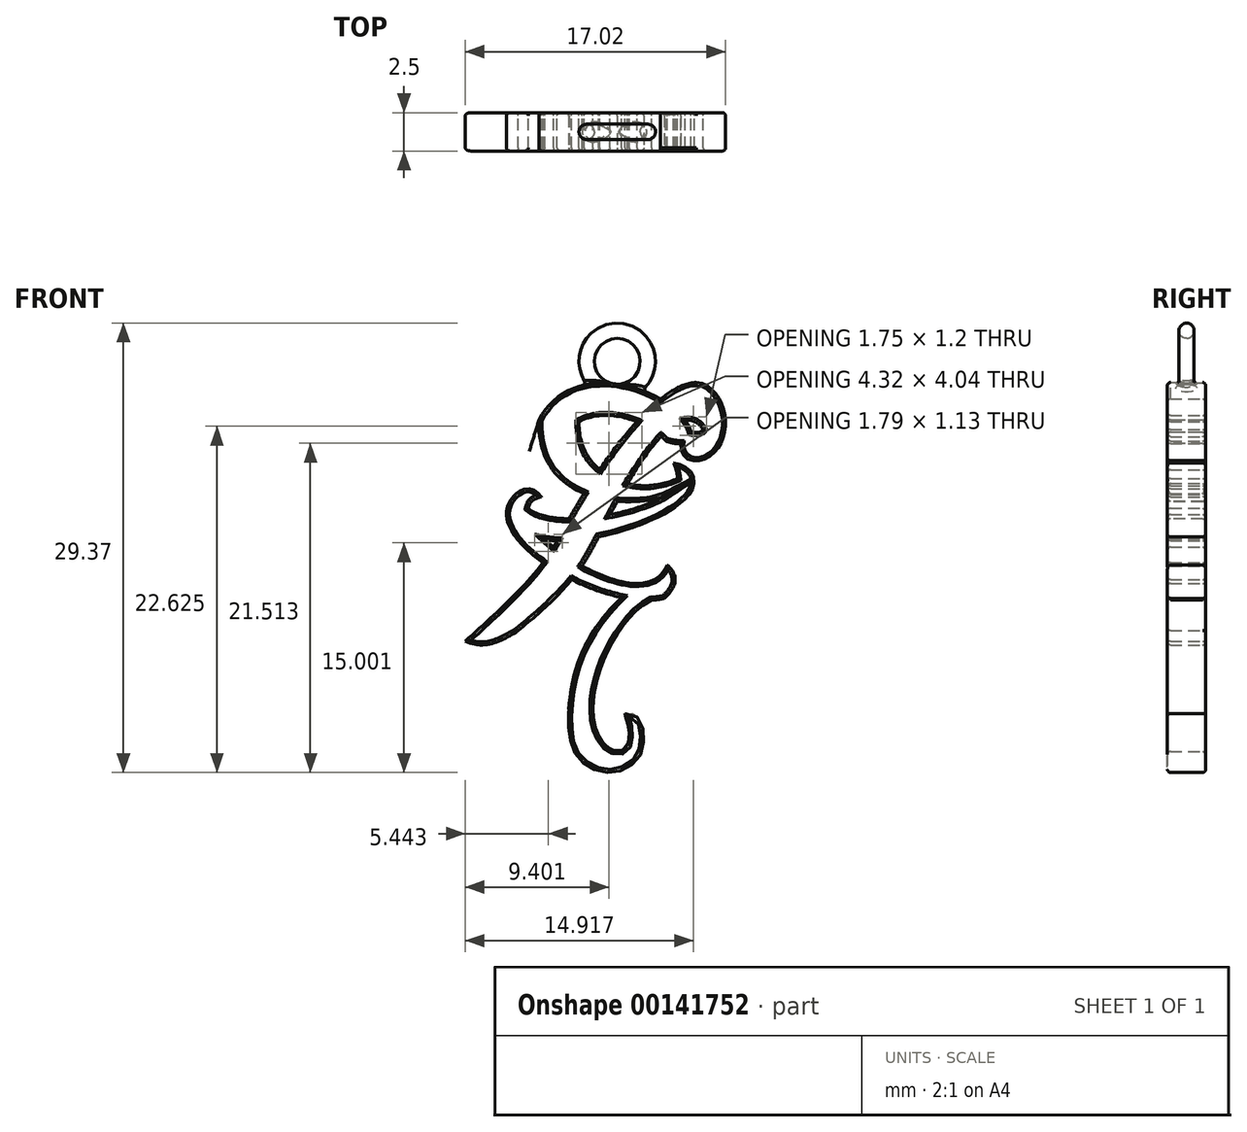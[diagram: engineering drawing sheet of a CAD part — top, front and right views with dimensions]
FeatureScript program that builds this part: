
annotation { "Feature Type Name" : "Feature", "Feature Type Description" : "" }
export const myFeature = defineFeature(function(context is Context, id is Id, definition is map)
    precondition{}
    {
        {
            var Q0;
            Q0=qCreatedBy(makeId("Front.planeOp"),FACE);
            var sketch = newSketch(context, id + "F0", { "sketchPlane" : qUnion([Q0])});
            skLineSegment(sketch, "E0.bottom", {"start": v(0, 0) * mm, "end": v(12.5, 0) * mm, "construction": true});
            skLineSegment(sketch, "E0.top", {"start": v(0, 25.5) * mm, "end": v(12.5, 25.5) * mm, "construction": true});
            skLineSegment(sketch, "E0.left", {"start": v(0, 0) * mm, "end": v(0, 25.5) * mm, "construction": true});
            skLineSegment(sketch, "E0.right", {"start": v(12.5, 0) * mm, "end": v(12.5, 25.5) * mm, "construction": true});
            skFitSpline(sketch, "E1", {"points": [v(0.5, 3.96) * mm, v(1.7, 1.95) * mm, v(0.92, 0.6) * mm, v(-0.5, 0.13) * mm, v(-2.58, 1.12) * mm, v(-3.17, 4.25) * mm, v(-2.44, 7.64) * mm, v(-1.46, 9.5) * mm, v(0.27, 11.56) * mm], "startDerivative": vector(27.69, 3.67) * mm, "endDerivative": vector(26.54, 27.1) * mm});
            skFitSpline(sketch, "E2", {"points": [v(-4.96, 18.14) * mm, v(-7.16, 17.54) * mm, v(-4.26, 13.45) * mm, v(3.06, 11.5) * mm], "startDerivative": vector(-9.5, 14) * mm, "endDerivative": vector(13.96, 3.31) * mm});
            skFitSpline(sketch, "E3", {"points": [v(3.06, 11.5) * mm, v(3.27, 13.69) * mm], "startDerivative": vector(2.83, 2.53) * mm, "endDerivative": vector(-2.14, 2) * mm});
            skFitSpline(sketch, "E4", {"points": [v(3.27, 13.69) * mm, v(-5.28, 15.92) * mm, v(-5.69, 17.73) * mm, v(-4.96, 18.14) * mm], "startDerivative": vector(-6.62, -15.9) * mm, "endDerivative": vector(7.8, 2.4) * mm});
            skFitSpline(sketch, "E5", {"points": [v(0.5, 3.96) * mm, v(0.46, 1.6) * mm, v(-0.56, 1.7) * mm, v(-1.47, 3.16) * mm, v(-1.45, 5.64) * mm, v(-0.38, 8.55) * mm, v(1.1, 10.57) * mm, v(2.25, 11.38) * mm], "startDerivative": vector(8.39, -21.65) * mm, "endDerivative": vector(12.87, 6.76) * mm});
            skFitSpline(sketch, "E6", {"points": [v(-5.82, 17.38) * mm, v(3.56, 18.52) * mm, v(3.9, 19.64) * mm, v(3.69, 20.36) * mm], "startDerivative": vector(9.43, -7.56) * mm, "endDerivative": vector(-2.6, 7.84) * mm});
            skFitSpline(sketch, "E7", {"points": [v(-4.74, 15.36) * mm, v(4.78, 18.4) * mm, v(3.69, 20.36) * mm], "startDerivative": vector(11.81, -2.43) * mm, "endDerivative": vector(-11.73, 2.21) * mm});
            skFitSpline(sketch, "E8", {"points": [v(3.25, 18.28) * mm, v(-5.12, 23.17) * mm], "startDerivative": vector(-5.6, -2.83) * mm, "endDerivative": vector(0.72, 17.36) * mm});
            skFitSpline(sketch, "E9", {"points": [v(3.95, 19.34) * mm, v(-2.5, 23.06) * mm], "startDerivative": vector(-9.08, -4.14) * mm, "endDerivative": vector(0.34, 10) * mm});
            skFitSpline(sketch, "E10", {"points": [v(-5.12, 23.17) * mm, v(4.83, 22.38) * mm], "startDerivative": vector(7.14, 13.52) * mm, "endDerivative": vector(2.17, -7.79) * mm});
            skFitSpline(sketch, "E11", {"points": [v(-2.5, 23.06) * mm, v(3.17, 21.8) * mm], "startDerivative": vector(5.66, 2.86) * mm, "endDerivative": vector(3.86, -4.07) * mm});
            skFitSpline(sketch, "E12", {"points": [v(3.17, 21.8) * mm, v(4.15, 21.6) * mm], "startDerivative": vector(0.91, -0.36) * mm, "endDerivative": vector(1.08, 0) * mm});
            skFitSpline(sketch, "E13", {"points": [v(4.83, 22.38) * mm, v(5.62, 22.54) * mm], "startDerivative": vector(0.9, -0.04) * mm, "endDerivative": vector(0.4, 0.77) * mm});
            skFitSpline(sketch, "E14", {"points": [v(4.15, 21.6) * mm, v(5.91, 20.7) * mm, v(7.03, 23.56) * mm, v(5.18, 25.62) * mm], "startDerivative": vector(-0.4, -12.26) * mm, "endDerivative": vector(-7.72, 0.04) * mm});
            skFitSpline(sketch, "E15", {"points": [v(5.62, 22.54) * mm, v(-0.36, 17.18) * mm, v(-6.48, 9.4) * mm], "startDerivative": vector(-9.74, 14.63) * mm, "endDerivative": vector(-24.26, -19.86) * mm});
            skFitSpline(sketch, "E16", {"points": [v(5.18, 25.62) * mm, v(-2.88, 17.18) * mm, v(-9.94, 8.7) * mm], "startDerivative": vector(-15.54, -0.02) * mm, "endDerivative": vector(-34.83, -31.36) * mm});
            skFitSpline(sketch, "E17", {"points": [v(-9.94, 8.7) * mm, v(-6.48, 9.4) * mm], "startDerivative": vector(2.4, -0.95) * mm, "endDerivative": vector(5.47, 3.65) * mm});
            skCircle(sketch, "E18", {"center": v(3.32, 3.06) * mm, "radius": 0.4 * mm, "construction": true});
            skSolve(sketch);
        }
        {
            var Q0;
            {var subQ0=sQuery(id+"F0.wireOp",EDGE,"E3");Q0=makeQuery(id+"F0.imprint","IMPRINT",FACE,{"disambiguationData":[TD([[makeQuery(id+"F0.imprint","IMPRINT",EDGE,{"derivedFrom":subQ0}),1.0]])]});}
            var Q1;
            {var subQ0=sQuery(id+"F0.wireOp",EDGE,"E1");Q1=makeQuery(id+"F0.imprint","IMPRINT",FACE,{"disambiguationData":[TD([[makeQuery(id+"F0.imprint","IMPRINT",EDGE,{"derivedFrom":subQ0}),-1.0]])]});}
            var Q2;
            {var subQ5=sQuery(id+"F0.wireOp",EDGE,"E17");Q2=makeQuery(id+"F0.imprint","IMPRINT",FACE,{"disambiguationData":[TD([[makeQuery(id+"F0.imprint","IMPRINT",EDGE,{"derivedFrom":subQ5}),1.0]])]});}
            var Q3;
            {var subQ0=sQuery(id+"F0.wireOp",EDGE,"E16");var subQ1=sQuery(id+"F0.wireOp",EDGE,"E2");var subQ2=makeQuery(id+"F0.imprint","INTERSECT",VERTEX,{"derivedFrom":[subQ1,subQ0]});Q3=makeQuery(id+"F0.imprint","IMPRINT",FACE,{"disambiguationData":[TD([[makeQuery(id+"F0.imprint","IMPRINT",EDGE,{"disambiguationData":[TD([[subQ2,-1.0]])],"derivedFrom":subQ1}),1.0]])]});}
            var Q4;
            {var subQ0=sQuery(id+"F0.wireOp",EDGE,"E4");var subQ5=sQuery(id+"F0.wireOp",EDGE,"E2");var subQ6=makeQuery(id+"F0.imprint","INTERSECT",VERTEX,{"derivedFrom":[subQ5,subQ0]});Q4=makeQuery(id+"F0.imprint","IMPRINT",FACE,{"disambiguationData":[TD([[makeQuery(id+"F0.imprint","IMPRINT",EDGE,{"disambiguationData":[TD([[subQ6,-1.0]])],"derivedFrom":subQ5}),1.0]])]});}
            var Q5;
            {var subQ0=sQuery(id+"F0.wireOp",EDGE,"E6");var subQ1=sQuery(id+"F0.wireOp",EDGE,"E4");var subQ2=makeQuery(id+"F0.imprint","INTERSECT",VERTEX,{"derivedFrom":[subQ1,subQ0]});Q5=makeQuery(id+"F0.imprint","IMPRINT",FACE,{"disambiguationData":[TD([[makeQuery(id+"F0.imprint","IMPRINT",EDGE,{"disambiguationData":[TD([[subQ2,1.0]])],"derivedFrom":subQ1}),-1.0]])]});}
            var Q6;
            {var subQ0=sQuery(id+"F0.wireOp",EDGE,"E15");var subQ1=sQuery(id+"F0.wireOp",EDGE,"E4");var subQ2=makeQuery(id+"F0.imprint","INTERSECT",VERTEX,{"derivedFrom":[subQ1,subQ0]});Q6=makeQuery(id+"F0.imprint","IMPRINT",FACE,{"disambiguationData":[TD([[makeQuery(id+"F0.imprint","IMPRINT",EDGE,{"disambiguationData":[TD([[subQ2,-1.0]])],"derivedFrom":subQ1}),-1.0]])]});}
            var Q7;
            {var subQ0=sQuery(id+"F0.wireOp",EDGE,"E16");var subQ1=sQuery(id+"F0.wireOp",EDGE,"E6");var subQ2=makeQuery(id+"F0.imprint","INTERSECT",VERTEX,{"derivedFrom":[subQ1,subQ0]});Q7=makeQuery(id+"F0.imprint","IMPRINT",FACE,{"disambiguationData":[TD([[makeQuery(id+"F0.imprint","IMPRINT",EDGE,{"disambiguationData":[TD([[subQ2,-1.0]])],"derivedFrom":subQ1}),-1.0]])]});}
            var Q8;
            {var subQ1=sQuery(id+"F0.wireOp",EDGE,"E6");var subQ4=makeQuery(id+"F0.imprint","INTERSECT",VERTEX,{"derivedFrom":[subQ1,sQuery(id+"F0.wireOp",EDGE,"E8")]});Q8=makeQuery(id+"F0.imprint","IMPRINT",FACE,{"disambiguationData":[TD([[makeQuery(id+"F0.imprint","IMPRINT",EDGE,{"disambiguationData":[TD([[subQ4,1.0]])],"derivedFrom":subQ1}),-1.0]])]});}
            var Q9;
            {var subQ0=sQuery(id+"F0.wireOp",EDGE,"E8");var subQ1=sQuery(id+"F0.wireOp",EDGE,"E6");var subQ2=makeQuery(id+"F0.imprint","INTERSECT",VERTEX,{"derivedFrom":[subQ1,subQ0]});Q9=makeQuery(id+"F0.imprint","IMPRINT",FACE,{"disambiguationData":[TD([[makeQuery(id+"F0.imprint","IMPRINT",EDGE,{"disambiguationData":[TD([[subQ2,-1.0]])],"derivedFrom":subQ1}),1.0]])]});}
            var Q10;
            {var subQ0=sQuery(id+"F0.wireOp",EDGE,"E16");var subQ1=sQuery(id+"F0.wireOp",EDGE,"E6");var subQ2=makeQuery(id+"F0.imprint","INTERSECT",VERTEX,{"derivedFrom":[subQ1,subQ0]});Q10=makeQuery(id+"F0.imprint","IMPRINT",FACE,{"disambiguationData":[TD([[makeQuery(id+"F0.imprint","IMPRINT",EDGE,{"disambiguationData":[TD([[subQ2,-1.0]])],"derivedFrom":subQ1}),1.0]])]});}
            var Q11;
            {var subQ0=sQuery(id+"F0.wireOp",EDGE,"E16");var subQ1=sQuery(id+"F0.wireOp",EDGE,"E8");var subQ2=makeQuery(id+"F0.imprint","INTERSECT",VERTEX,{"derivedFrom":[subQ1,subQ0]});Q11=makeQuery(id+"F0.imprint","IMPRINT",FACE,{"disambiguationData":[TD([[makeQuery(id+"F0.imprint","IMPRINT",EDGE,{"disambiguationData":[TD([[subQ2,1.0]])],"derivedFrom":subQ1}),-1.0]])]});}
            var Q12;
            {var subQ5=sQuery(id+"F0.wireOp",EDGE,"E10");var subQ6=sQuery(id+"F0.wireOp",EDGE,"E8");var subQ7=makeQuery(id+"F0.imprint","INTERSECT",VERTEX,{"derivedFrom":[subQ6,subQ5]});Q12=makeQuery(id+"F0.imprint","IMPRINT",FACE,{"disambiguationData":[TD([[makeQuery(id+"F0.imprint","IMPRINT",EDGE,{"disambiguationData":[TD([[subQ7,1.0]])],"derivedFrom":subQ6}),-1.0]])]});}
            var Q13;
            {var subQ0=sQuery(id+"F0.wireOp",EDGE,"E15");var subQ1=sQuery(id+"F0.wireOp",EDGE,"E9");var subQ2=makeQuery(id+"F0.imprint","INTERSECT",VERTEX,{"derivedFrom":[subQ1,subQ0]});Q13=makeQuery(id+"F0.imprint","IMPRINT",FACE,{"disambiguationData":[TD([[makeQuery(id+"F0.imprint","IMPRINT",EDGE,{"disambiguationData":[TD([[subQ2,-1.0]])],"derivedFrom":subQ1}),-1.0]])]});}
            var Q14;
            {var subQ0=sQuery(id+"F0.wireOp",EDGE,"E16");var subQ1=sQuery(id+"F0.wireOp",EDGE,"E10");var subQ2=makeQuery(id+"F0.imprint","INTERSECT",VERTEX,{"derivedFrom":[subQ1,subQ0]});Q14=makeQuery(id+"F0.imprint","IMPRINT",FACE,{"disambiguationData":[TD([[makeQuery(id+"F0.imprint","IMPRINT",EDGE,{"disambiguationData":[TD([[subQ2,-1.0]])],"derivedFrom":subQ1}),-1.0]])]});}
            var Q15;
            {var subQ0=sQuery(id+"F0.wireOp",EDGE,"E12");Q15=makeQuery(id+"F0.imprint","IMPRINT",FACE,{"disambiguationData":[TD([[makeQuery(id+"F0.imprint","IMPRINT",EDGE,{"derivedFrom":subQ0}),1.0]])]});}
            extrude(context, id + "F1", {"entities" : qUnion([Q0, Q1, Q2, Q3, Q4, Q5, Q6, Q7, Q8, Q9, Q10, Q11, Q12, Q13, Q14, Q15]), "depth" : 1.25 * mm, "offsetDistance" : 25 * mm, "hasSecondDirection" : true, "secondDirectionOppositeDirection" : true, "secondDirectionDepth" : 1.25 * mm});
        }
        {
            var Q0;
            Q0=makeQuery(id+"F1.opExtrude","CAP_EDGE",EDGE,{"disambiguationData":[OSD([sQuery(id+"F0.wireOp",EDGE,"4681fdc7-3070-4394-86cc-40bf6d9edfaf")])],"isStart":false});
            var Q1;
            Q1=makeQuery(id+"F1.opExtrude","CAP_FACE",FACE,{"disambiguationData":[OSD([sQuery(id+"F0.wireOp",EDGE,"4681fdc7-3070-4394-86cc-40bf6d9edfaf"),sQuery(id+"F0.wireOp",EDGE,"8c27ad56-a9f0-494b-b41c-2942c247f4c6"),sQuery(id+"F0.wireOp",EDGE,"f5e0758e-03f0-4c22-9960-8cbbef7d2f47"),sQuery(id+"F0.wireOp",EDGE,"3a872d37-1245-47a6-877a-3f2e58ba2b5f"),sQuery(id+"F0.wireOp",EDGE,"DYU3Zu34-DmmR-dnbN-u9n5-0PIQUu0Xy99a"),sQuery(id+"F0.wireOp",EDGE,"28485420-370c-429b-b7ea-971533ee887e"),sQuery(id+"F0.wireOp",EDGE,"E1"),sQuery(id+"F0.wireOp",EDGE,"b2d6f1f3-02ad-49aa-b6fe-aaa647de590c"),sQuery(id+"F0.wireOp",EDGE,"E2"),sQuery(id+"F0.wireOp",EDGE,"E3"),sQuery(id+"F0.wireOp",EDGE,"5b510dd0-313c-4d0d-92ab-dbbb8d0ca943"),sQuery(id+"F0.wireOp",EDGE,"E4")])],"isStart":false});
            var Q2;
            Q2=makeQuery(id+"F1.opExtrude","CAP_FACE",FACE,{"disambiguationData":[OSD([sQuery(id+"F0.wireOp",EDGE,"4681fdc7-3070-4394-86cc-40bf6d9edfaf"),sQuery(id+"F0.wireOp",EDGE,"8c27ad56-a9f0-494b-b41c-2942c247f4c6"),sQuery(id+"F0.wireOp",EDGE,"f5e0758e-03f0-4c22-9960-8cbbef7d2f47"),sQuery(id+"F0.wireOp",EDGE,"3a872d37-1245-47a6-877a-3f2e58ba2b5f"),sQuery(id+"F0.wireOp",EDGE,"DYU3Zu34-DmmR-dnbN-u9n5-0PIQUu0Xy99a"),sQuery(id+"F0.wireOp",EDGE,"28485420-370c-429b-b7ea-971533ee887e"),sQuery(id+"F0.wireOp",EDGE,"E1"),sQuery(id+"F0.wireOp",EDGE,"b2d6f1f3-02ad-49aa-b6fe-aaa647de590c"),sQuery(id+"F0.wireOp",EDGE,"E2"),sQuery(id+"F0.wireOp",EDGE,"E3"),sQuery(id+"F0.wireOp",EDGE,"5b510dd0-313c-4d0d-92ab-dbbb8d0ca943"),sQuery(id+"F0.wireOp",EDGE,"E4")])],"isStart":true});
            fillet(context, id + "F2", {"entities" : qUnion([Q0, Q1, Q2]), "tangentPropagation" : true, "radius" : 0.2 * mm, "defaultsChanged" : false, "vertexSettings" : [], "allowEdgeOverflow" : false});
        }
        {
            var Q0;
            Q0=qCreatedBy(makeId("Right.planeOp"),FACE);
            var sketch = newSketch(context, id + "F3", { "sketchPlane" : qUnion([Q0])});
            skCircle(sketch, "E19", {"center": v(0, 25) * mm, "radius": 0.5 * mm});
            skLineSegment(sketch, "E20", {"start": v(-3.3, 27) * mm, "end": v(3.34, 27) * mm, "construction": true});
            skSolve(sketch);
        }
        {
            var Q0;
            Q0=qSketchRegion(id+"F3",true);
            var Q1;
            Q1=sQuery(id+"F3.wireOp",EDGE,"E20");
            revolve(context, id + "F4", {"operationType" : NewBodyOperationType.ADD, "surfaceOperationType" : NewSurfaceOperationType.NEW, "entities" : qUnion([Q0]), "axis" : qUnion([Q1]), "revolveType" : RevolveType.FULL});
        }
        {
            var Q0;
            {var subQ0=sQuery(id+"F0.wireOp",EDGE,"E10");Q0=makeQuery(id+"F4.boolean.opBoolean","INTERSECT",EDGE,{"disambiguationData":[OD(0.0)],"derivedFrom":[makeQuery(id+"F1.opExtrude","SWEPT_FACE",FACE,{"disambiguationData":[OSD([subQ0]),TDD([makeQuery(id+"F0.imprint","IMPRINT",EDGE,{"disambiguationData":[TD([[makeQuery(id+"F0.imprint","INTERSECT",VERTEX,{"derivedFrom":[sQuery(id+"F0.wireOp",EDGE,"E8"),subQ0]}),-1.0]])],"derivedFrom":subQ0})])]}),makeQuery(id+"F4.opRevolve","SWEPT_FACE",FACE,{"disambiguationData":[OSD([sQuery(id+"F3.wireOp",EDGE,"E19")])]})]});}
            var Q1;
            {var subQ0=sQuery(id+"F0.wireOp",EDGE,"E10");Q1=makeQuery(id+"F4.boolean.opBoolean","INTERSECT",EDGE,{"disambiguationData":[OD(1.0)],"derivedFrom":[makeQuery(id+"F1.opExtrude","SWEPT_FACE",FACE,{"disambiguationData":[OSD([subQ0]),TDD([makeQuery(id+"F0.imprint","IMPRINT",EDGE,{"disambiguationData":[TD([[makeQuery(id+"F0.imprint","INTERSECT",VERTEX,{"derivedFrom":[sQuery(id+"F0.wireOp",EDGE,"E8"),subQ0]}),-1.0]])],"derivedFrom":subQ0})])]}),makeQuery(id+"F4.opRevolve","SWEPT_FACE",FACE,{"disambiguationData":[OSD([sQuery(id+"F3.wireOp",EDGE,"E19")])]})]});}
            fillet(context, id + "F5", {"entities" : qUnion([Q0, Q1]), "tangentPropagation" : true, "radius" : 0.2 * mm, "defaultsChanged" : true, "vertexSettings" : [], "allowEdgeOverflow" : false});
        }
    });
